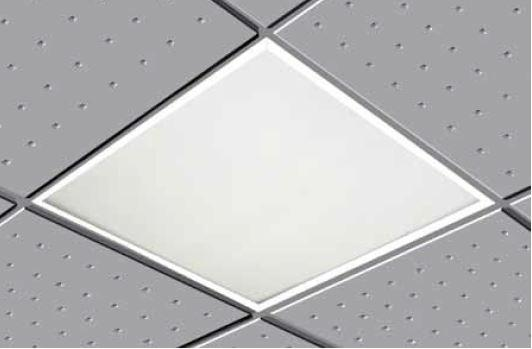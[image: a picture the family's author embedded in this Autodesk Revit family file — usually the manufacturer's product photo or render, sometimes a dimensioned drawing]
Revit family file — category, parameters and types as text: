
# Revit family: G 6060 OPT
name_source: partatom
category: Lighting Fixtures
revit_build: Autodesk Revit 2017 (Build: 20160225_1515(x64)
units: mm (PartAtom-declared; Revit-internal decimal feet)

## family parameters
Always vertical = Yes
Cut with Voids When Loaded = No
Host = Ceiling
Light Source = Yes
OmniClass Number = 23.80.70.11
OmniClass Title = Luminaries for Internal Lighting
Part Type = Normal
Room Calculation Point = No
Round Connector Dimension = Use Diameter
Shared = No

## types (2) — shared parameters
Apparent Load = 36 VA
Color Filter = 16777215
Dimming Lamp Color Temperature Shift = <None>
Emit Shape Visible in Rendering = Yes
Emit from Rectangle Length = 530 mm  [stored 1.73885 ft]
Emit from Rectangle Width = 530 mm  [stored 1.73885 ft]
Light Source Symbol Size = 610 mm
Manufacturer = ARLIGHT
Type Image = G 6060 OPT.JPG
Wattage Comments = 36

## type names (no varying parameters)
- GOPT.6060.36.30
- GOPT.6060.36.40

note: [stored X ft] marks values corroborated as IEEE doubles in the binary element streams (Revit-internal decimal feet)

## geometry (parser evidence)
native form markers: Sweep x2
no freeform markers — native parametric forms only
